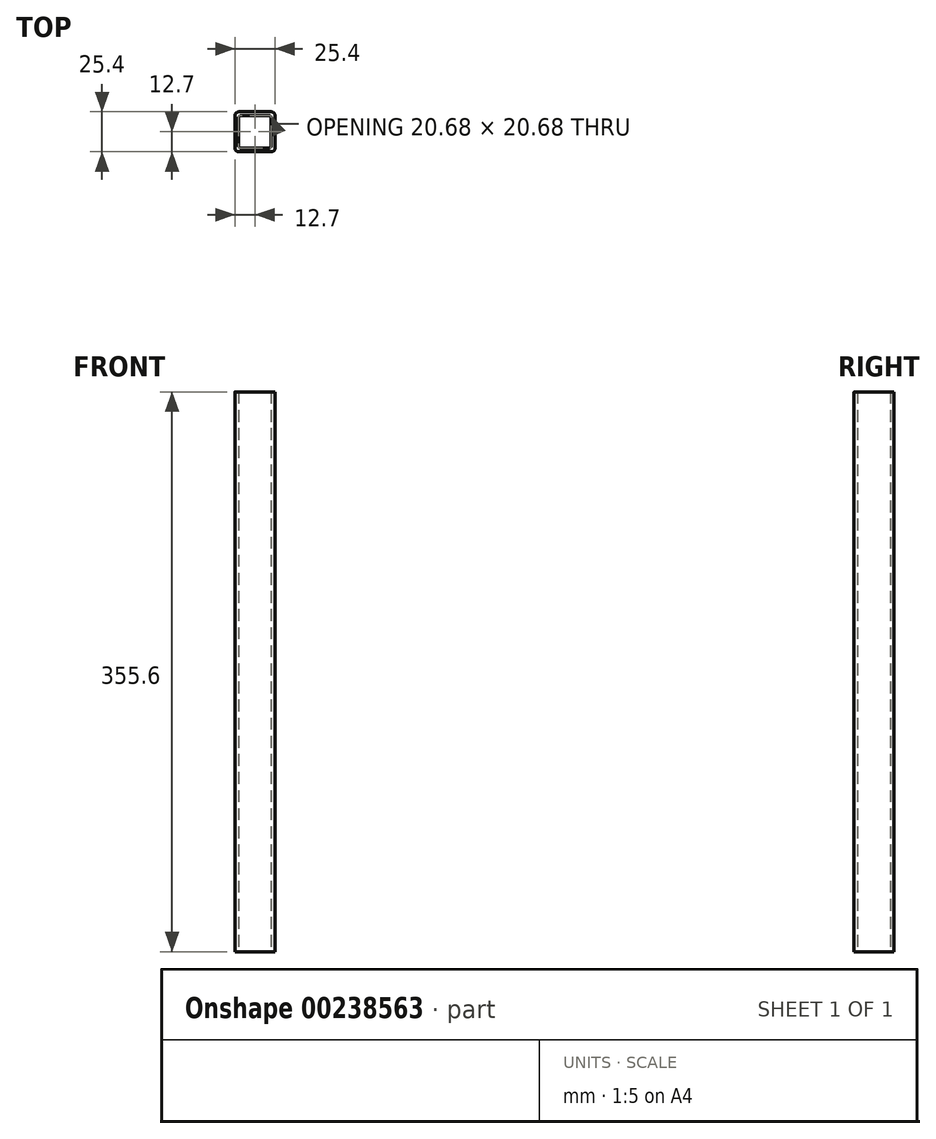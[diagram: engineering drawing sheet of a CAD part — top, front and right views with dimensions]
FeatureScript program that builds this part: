
annotation { "Feature Type Name" : "Feature", "Feature Type Description" : "" }
export const myFeature = defineFeature(function(context is Context, id is Id, definition is map)
    precondition{}
    {
        {
            var Q0;
            Q0=qCreatedBy(makeId("Top.planeOp"),FACE);
            var sketch = newSketch(context, id + "F0", { "sketchPlane" : qUnion([Q0])});
            skLineSegment(sketch, "E0", {"start": v(-12.7, 10.34) * mm, "end": v(-12.7, -10.34) * mm});
            skLineSegment(sketch, "E1", {"start": v(-10.34, -12.7) * mm, "end": v(10.34, -12.7) * mm});
            skLineSegment(sketch, "E2", {"start": v(12.7, -10.34) * mm, "end": v(12.7, 10.34) * mm});
            skLineSegment(sketch, "E3", {"start": v(10.34, 12.7) * mm, "end": v(-10.34, 12.7) * mm});
            skLineSegment(sketch, "E4", {"start": v(0, 12.7) * mm, "end": v(0, -12.7) * mm, "construction": true});
            skLineSegment(sketch, "E5", {"start": v(-12.7, 0) * mm, "end": v(12.7, 0) * mm, "construction": true});
            skPoint(sketch, "E6", {"position": v(0, 0) * mm});
            skPoint(sketch, "E7.visualSharp", {"position": v(-12.7, 12.7) * mm});
            skArc(sketch, "E7.filletArc", {"start": v(-10.34, 12.7) * mm, "mid": v(-12, 12) * mm, "end": v(-12.7, 10.34) * mm});
            skPoint(sketch, "E8.visualSharp", {"position": v(12.7, 12.7) * mm});
            skArc(sketch, "E8.filletArc", {"start": v(12.7, 10.34) * mm, "mid": v(12, 12) * mm, "end": v(10.34, 12.7) * mm});
            skPoint(sketch, "E9.visualSharp", {"position": v(12.7, -12.7) * mm});
            skArc(sketch, "E9.filletArc", {"start": v(10.34, -12.7) * mm, "mid": v(12, -12) * mm, "end": v(12.7, -10.34) * mm});
            skPoint(sketch, "E10.visualSharp", {"position": v(-12.7, -12.7) * mm});
            skArc(sketch, "E10.filletArc", {"start": v(-12.7, -10.34) * mm, "mid": v(-12, -12) * mm, "end": v(-10.34, -12.7) * mm});
            skLineSegment(sketch, "E11.0", {"start": v(8.81, 10.34) * mm, "end": v(-8.81, 10.34) * mm});
            skLineSegment(sketch, "E12.0", {"start": v(10.34, -8.81) * mm, "end": v(10.34, 8.81) * mm});
            skLineSegment(sketch, "E13.0", {"start": v(-8.81, -10.34) * mm, "end": v(8.81, -10.34) * mm});
            skLineSegment(sketch, "E14.0", {"start": v(-10.34, 8.81) * mm, "end": v(-10.34, -8.81) * mm});
            skArc(sketch, "E15.filletArc", {"start": v(-8.81, 10.34) * mm, "mid": v(-9.9, 9.9) * mm, "end": v(-10.34, 8.81) * mm});
            skArc(sketch, "E16.filletArc", {"start": v(10.34, 8.81) * mm, "mid": v(9.9, 9.9) * mm, "end": v(8.81, 10.34) * mm});
            skArc(sketch, "E17.filletArc", {"start": v(8.81, -10.34) * mm, "mid": v(9.9, -9.9) * mm, "end": v(10.34, -8.81) * mm});
            skArc(sketch, "E18.filletArc", {"start": v(-10.34, -8.81) * mm, "mid": v(-9.9, -9.9) * mm, "end": v(-8.81, -10.34) * mm});
            skSolve(sketch);
        }
        {
            var Q0;
            Q0=makeQuery(id+"F0.imprint","IMPRINT",FACE,{"disambiguationData":[TD([[makeQuery(id+"F0.imprint","IMPRINT",EDGE,{"derivedFrom":sQuery(id+"F0.wireOp",EDGE,"E0")}),1.0]])]});
            extrude(context, id + "F1", {"entities" : qUnion([Q0]), "depth" : 355.6 * mm});
        }
    });
